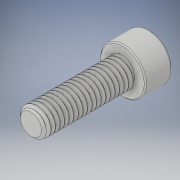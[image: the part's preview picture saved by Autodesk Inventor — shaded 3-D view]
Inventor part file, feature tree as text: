
AUTODESK INVENTOR PART (.ipt)
format: ipt  version: 2018 (Build 220112000, 112)  size: 848,896 bytes
history: native  units: in
note: dims shown in document units (in); Inventor stores cm internally (conversion verified against a paired STEP export)
features: chamfer x1
ambient origin geometry x8: Origin, YZ Plane, XZ Plane, XY Plane, X Axis, Y Axis, Z Axis, Center Point
bodies: Solid1 (feature_tree)
feature tree (1):
  chamfer  "Chamfer2"  [1 undecoded]
note: 1 required parameter value undecoded (feature->parameter linkage not recoverable at this tier; creation-order binding heuristic only, values carry confidence <= 0.55)
